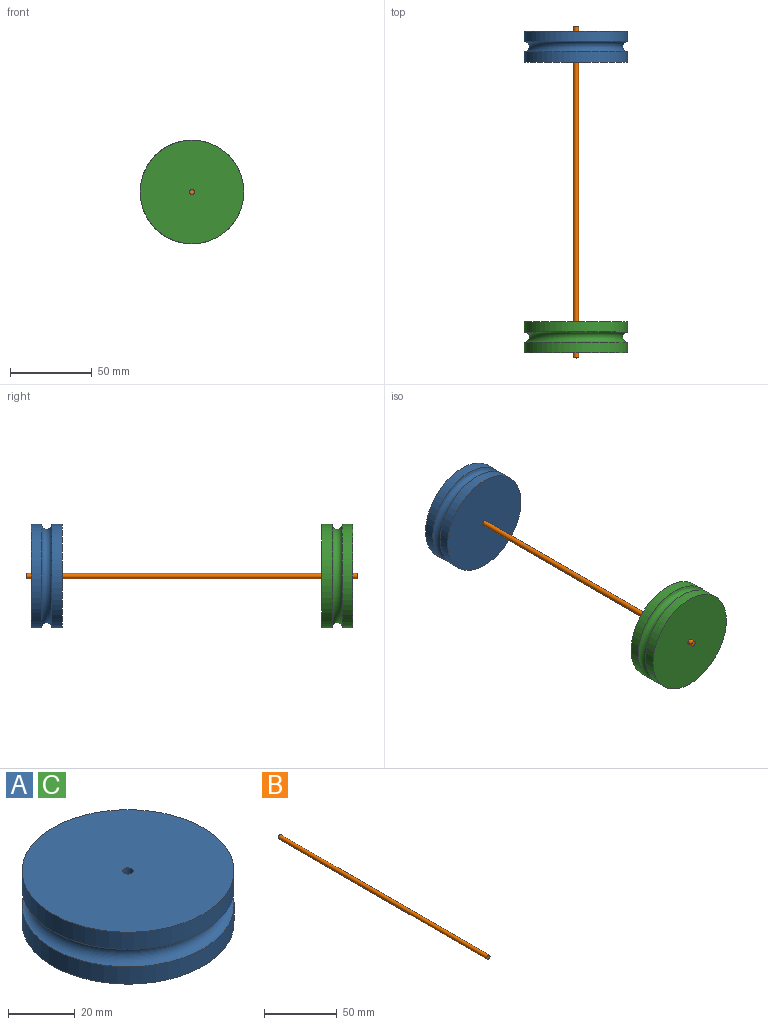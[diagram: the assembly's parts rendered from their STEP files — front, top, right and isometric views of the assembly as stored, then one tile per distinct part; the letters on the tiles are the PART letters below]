
ASSEMBLY  parts=3 mates=1
PART A: 6 faces, bbox 73.6x73.6x19.1 mm
  f0: cylinder r=31.75mm len=63.5mm, axis (0,0,-1), area 1266.8mm2, adj f2,f5
  f1: cylinder r=31.75mm len=63.5mm, axis (0,0,-1), area 1266.8mm2, adj f3,f5
  f2: plane 63.5x63.5mm, normal (0,0,1), area 3159mm2, adj f0,f4
  f3: plane 63.5x63.5mm, normal (0,0,-1), area 3159mm2, adj f1,f4
  f4: cylinder r=1.59mm len=19.05mm, axis (0,0,-1), area 190mm2, adj f2,f3
  f5: torus R=31.75mm, axis (0,0,1), area 1863.2mm2, adj f0,f1
PART B: 3 faces, bbox 3.2x203.2x3.2 mm
  f0: cylinder r=1.59mm len=203.2mm, axis (0,1,0), area 2026.8mm2, adj f1,f2
  f1: plane 3.18x3.18mm, normal (0,-1,0), area 7.9mm2, adj f0
  f2: plane 3.18x3.18mm, normal (0,1,0), area 7.9mm2, adj f0
PART C: same geometry as A
PLACE A rot(axis=(1,0,0),90deg) t=(-7.72,60.18,11.61)mm
PLACE B t=(-7.72,-28.72,11.61)mm
PLACE C rot(axis=(1,0,0),90deg) t=(-7.72,-117.62,11.61)mm
MATE revolute A.f4 <-> B.f0  axis (0,1,0) through (-7.72,60.18,11.61)mm
